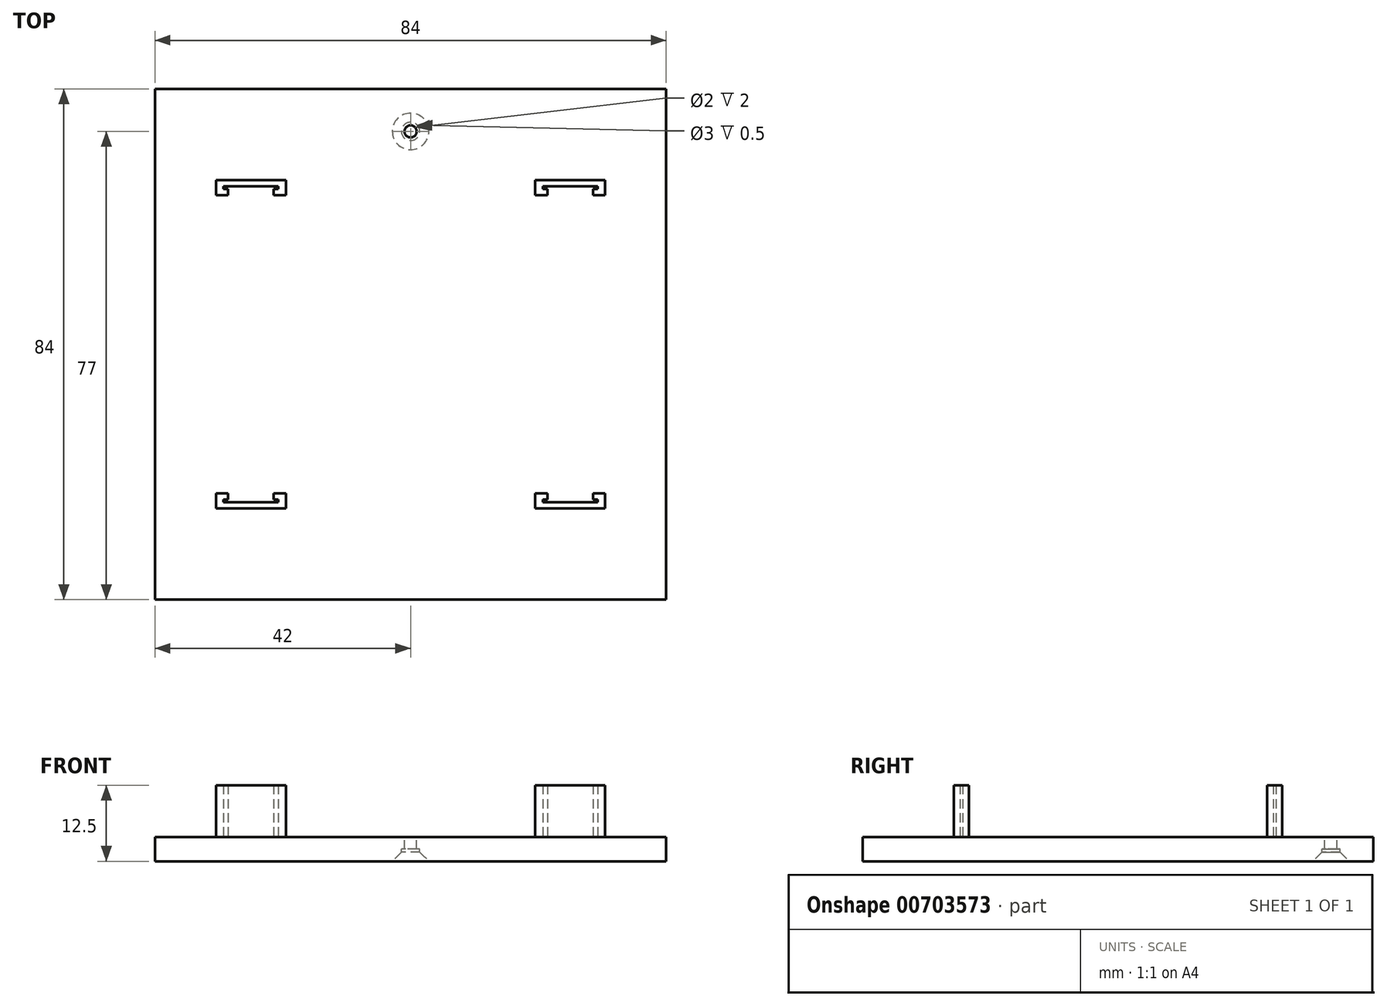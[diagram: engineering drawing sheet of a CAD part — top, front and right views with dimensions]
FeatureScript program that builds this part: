
annotation { "Feature Type Name" : "Feature", "Feature Type Description" : "" }
export const myFeature = defineFeature(function(context is Context, id is Id, definition is map)
    precondition{}
    {
        {
            var Q0;
            Q0=qCreatedBy(makeId("Top.planeOp"),FACE);
            var sketch = newSketch(context, id + "F0", { "sketchPlane" : qUnion([Q0])});
            skLineSegment(sketch, "E0.bottom", {"start": v(-42, 42) * mm, "end": v(42, 42) * mm});
            skLineSegment(sketch, "E0.top", {"start": v(-42, -42) * mm, "end": v(42, -42) * mm});
            skLineSegment(sketch, "E0.left", {"start": v(-42, 42) * mm, "end": v(-42, -42) * mm});
            skLineSegment(sketch, "E0.right", {"start": v(42, 42) * mm, "end": v(42, -42) * mm});
            skSolve(sketch);
        }
        {
            var Q0;
            Q0 = qSketchRegion(id + "F0", true);
            var Q1;
            Q1=makeQuery(id+"F0.imprint","IMPRINT",FACE,{"disambiguationData":[TD([[makeQuery(id+"F0.imprint","IMPRINT",EDGE,{"derivedFrom":sQuery(id+"F0.wireOp",EDGE,"E0.bottom")}),-1.0]])]});
            extrude(context, id + "F1", {"entities" : qUnion([Q0, Q1]), "depth" : 4 * mm, "offsetDistance" : 25 * mm});
        }
        {
            var Q0;
            Q0=makeQuery(id+"F1.opExtrude","CAP_FACE",FACE,{"disambiguationData":[OSD([sQuery(id+"F0.wireOp",EDGE,"E0.bottom"),sQuery(id+"F0.wireOp",EDGE,"E0.top"),sQuery(id+"F0.wireOp",EDGE,"E0.left"),sQuery(id+"F0.wireOp",EDGE,"E0.right")])],"isStart":false});
            var sketch = newSketch(context, id + "F2", { "sketchPlane" : qUnion([Q0])});
            skLineSegment(sketch, "E1.bottom", {"start": v(-32, 27) * mm, "end": v(-30, 27) * mm});
            skLineSegment(sketch, "E1.top", {"start": v(-32, 24.5) * mm, "end": v(-30, 24.5) * mm});
            skLineSegment(sketch, "E1.left", {"start": v(-32, 27) * mm, "end": v(-32, 24.5) * mm});
            skLineSegment(sketch, "E1.right", {"start": v(-30, 27) * mm, "end": v(-30, 24.5) * mm});
            skLineSegment(sketch, "E2.bottom", {"start": v(-22.5, 27) * mm, "end": v(-20.5, 27) * mm});
            skLineSegment(sketch, "E2.top", {"start": v(-22.5, 24.5) * mm, "end": v(-20.5, 24.5) * mm});
            skLineSegment(sketch, "E2.left", {"start": v(-22.5, 27) * mm, "end": v(-22.5, 24.5) * mm});
            skLineSegment(sketch, "E2.right", {"start": v(-20.5, 27) * mm, "end": v(-20.5, 24.5) * mm});
            skLineSegment(sketch, "E3", {"start": v(-30, 27) * mm, "end": v(-22.5, 27) * mm});
            skLineSegment(sketch, "E4", {"start": v(-30, 25.5) * mm, "end": v(-22.5, 25.5) * mm, "construction": true});
            skLineSegment(sketch, "E5", {"start": v(-30, 26) * mm, "end": v(-22.5, 26) * mm});
            skLineSegment(sketch, "E6", {"start": v(-30, 26) * mm, "end": v(-30.75, 26) * mm});
            skLineSegment(sketch, "E7", {"start": v(-30.75, 26) * mm, "end": v(-30.75, 25.5) * mm});
            skLineSegment(sketch, "E8", {"start": v(-30.75, 25.5) * mm, "end": v(-30, 25.5) * mm});
            skLineSegment(sketch, "E9", {"start": v(-22.5, 26) * mm, "end": v(-21.75, 26) * mm});
            skLineSegment(sketch, "E10", {"start": v(-21.75, 26) * mm, "end": v(-21.75, 25.5) * mm});
            skLineSegment(sketch, "E11", {"start": v(-21.75, 25.5) * mm, "end": v(-22.5, 25.5) * mm});
            skLineSegment(sketch, "E12.bottom", {"start": v(-20.5, -27) * mm, "end": v(-22.5, -27) * mm});
            skLineSegment(sketch, "E12.top", {"start": v(-20.5, -24.5) * mm, "end": v(-22.5, -24.5) * mm});
            skLineSegment(sketch, "E12.left", {"start": v(-20.5, -27) * mm, "end": v(-20.5, -24.5) * mm});
            skLineSegment(sketch, "E12.right", {"start": v(-22.5, -27) * mm, "end": v(-22.5, -24.5) * mm});
            skLineSegment(sketch, "E13.bottom", {"start": v(-30, -27) * mm, "end": v(-32, -27) * mm});
            skLineSegment(sketch, "E13.top", {"start": v(-30, -24.5) * mm, "end": v(-32, -24.5) * mm});
            skLineSegment(sketch, "E13.left", {"start": v(-30, -27) * mm, "end": v(-30, -24.5) * mm});
            skLineSegment(sketch, "E13.right", {"start": v(-32, -27) * mm, "end": v(-32, -24.5) * mm});
            skLineSegment(sketch, "E14", {"start": v(-22.5, -27) * mm, "end": v(-30, -27) * mm});
            skLineSegment(sketch, "E15", {"start": v(-22.5, -25.5) * mm, "end": v(-30, -25.5) * mm, "construction": true});
            skLineSegment(sketch, "E16", {"start": v(-22.5, -26) * mm, "end": v(-30, -26) * mm});
            skLineSegment(sketch, "E17", {"start": v(-22.5, -26) * mm, "end": v(-21.75, -26) * mm});
            skLineSegment(sketch, "E18", {"start": v(-21.75, -26) * mm, "end": v(-21.75, -25.5) * mm});
            skLineSegment(sketch, "E19", {"start": v(-21.75, -25.5) * mm, "end": v(-22.5, -25.5) * mm});
            skLineSegment(sketch, "E20", {"start": v(-30, -26) * mm, "end": v(-30.75, -26) * mm});
            skLineSegment(sketch, "E21", {"start": v(-30.75, -26) * mm, "end": v(-30.75, -25.5) * mm});
            skLineSegment(sketch, "E22", {"start": v(-30.75, -25.5) * mm, "end": v(-30, -25.5) * mm});
            skLineSegment(sketch, "E23", {"start": v(-32, 24.5) * mm, "end": v(-32, -24.5) * mm, "construction": true});
            skLineSegment(sketch, "E24.bottom", {"start": v(20.5, 27) * mm, "end": v(22.5, 27) * mm});
            skLineSegment(sketch, "E24.top", {"start": v(20.5, 24.5) * mm, "end": v(22.5, 24.5) * mm});
            skLineSegment(sketch, "E24.left", {"start": v(20.5, 27) * mm, "end": v(20.5, 24.5) * mm});
            skLineSegment(sketch, "E24.right", {"start": v(22.5, 27) * mm, "end": v(22.5, 24.5) * mm});
            skLineSegment(sketch, "E25.bottom", {"start": v(30, 27) * mm, "end": v(32, 27) * mm});
            skLineSegment(sketch, "E25.top", {"start": v(30, 24.5) * mm, "end": v(32, 24.5) * mm});
            skLineSegment(sketch, "E25.left", {"start": v(30, 27) * mm, "end": v(30, 24.5) * mm});
            skLineSegment(sketch, "E25.right", {"start": v(32, 27) * mm, "end": v(32, 24.5) * mm});
            skLineSegment(sketch, "E26", {"start": v(22.5, 27) * mm, "end": v(30, 27) * mm});
            skLineSegment(sketch, "E27", {"start": v(22.5, 25.5) * mm, "end": v(30, 25.5) * mm, "construction": true});
            skLineSegment(sketch, "E28", {"start": v(22.5, 26) * mm, "end": v(30, 26) * mm});
            skLineSegment(sketch, "E29", {"start": v(22.5, 26) * mm, "end": v(21.75, 26) * mm});
            skLineSegment(sketch, "E30", {"start": v(21.75, 26) * mm, "end": v(21.75, 25.5) * mm});
            skLineSegment(sketch, "E31", {"start": v(21.75, 25.5) * mm, "end": v(22.5, 25.5) * mm});
            skLineSegment(sketch, "E32", {"start": v(30, 26) * mm, "end": v(30.75, 26) * mm});
            skLineSegment(sketch, "E33", {"start": v(30.75, 26) * mm, "end": v(30.75, 25.5) * mm});
            skLineSegment(sketch, "E34", {"start": v(30.75, 25.5) * mm, "end": v(30, 25.5) * mm});
            skLineSegment(sketch, "E35.bottom", {"start": v(32, -27) * mm, "end": v(30, -27) * mm});
            skLineSegment(sketch, "E35.top", {"start": v(32, -24.5) * mm, "end": v(30, -24.5) * mm});
            skLineSegment(sketch, "E35.left", {"start": v(32, -27) * mm, "end": v(32, -24.5) * mm});
            skLineSegment(sketch, "E35.right", {"start": v(30, -27) * mm, "end": v(30, -24.5) * mm});
            skLineSegment(sketch, "E36.bottom", {"start": v(22.5, -27) * mm, "end": v(20.5, -27) * mm});
            skLineSegment(sketch, "E36.top", {"start": v(22.5, -24.5) * mm, "end": v(20.5, -24.5) * mm});
            skLineSegment(sketch, "E36.left", {"start": v(22.5, -27) * mm, "end": v(22.5, -24.5) * mm});
            skLineSegment(sketch, "E36.right", {"start": v(20.5, -27) * mm, "end": v(20.5, -24.5) * mm});
            skLineSegment(sketch, "E37", {"start": v(30, -27) * mm, "end": v(22.5, -27) * mm});
            skLineSegment(sketch, "E38", {"start": v(30, -25.5) * mm, "end": v(22.5, -25.5) * mm, "construction": true});
            skLineSegment(sketch, "E39", {"start": v(30, -26) * mm, "end": v(22.5, -26) * mm});
            skLineSegment(sketch, "E40", {"start": v(30, -26) * mm, "end": v(30.75, -26) * mm});
            skLineSegment(sketch, "E41", {"start": v(30.75, -26) * mm, "end": v(30.75, -25.5) * mm});
            skLineSegment(sketch, "E42", {"start": v(30.75, -25.5) * mm, "end": v(30, -25.5) * mm});
            skLineSegment(sketch, "E43", {"start": v(22.5, -26) * mm, "end": v(21.75, -26) * mm});
            skLineSegment(sketch, "E44", {"start": v(21.75, -26) * mm, "end": v(21.75, -25.5) * mm});
            skLineSegment(sketch, "E45", {"start": v(21.75, -25.5) * mm, "end": v(22.5, -25.5) * mm});
            skLineSegment(sketch, "E46", {"start": v(20.5, 24.5) * mm, "end": v(20.5, -24.5) * mm, "construction": true});
            skLineSegment(sketch, "E47", {"start": v(-20.5, 27) * mm, "end": v(20.5, 27) * mm, "construction": true});
            skSolve(sketch);
        }
        {
            var Q0;
            {var subQ1=sQuery(id+"F2.wireOp",EDGE,"E1.bottom");Q0=makeQuery(id+"F2.imprint","IMPRINT",FACE,{"disambiguationData":[TD([[makeQuery(id+"F2.imprint","IMPRINT",EDGE,{"derivedFrom":subQ1}),-1.0]])]});}
            var Q1;
            {var subQ0=sQuery(id+"F2.wireOp",EDGE,"E3");Q1=makeQuery(id+"F2.imprint","IMPRINT",FACE,{"disambiguationData":[TD([[makeQuery(id+"F2.imprint","IMPRINT",EDGE,{"derivedFrom":subQ0}),-1.0]])]});}
            var Q2;
            {var subQ3=sQuery(id+"F2.wireOp",EDGE,"E2.bottom");Q2=makeQuery(id+"F2.imprint","IMPRINT",FACE,{"disambiguationData":[TD([[makeQuery(id+"F2.imprint","IMPRINT",EDGE,{"derivedFrom":subQ3}),-1.0]])]});}
            var Q3;
            {var subQ3=sQuery(id+"F2.wireOp",EDGE,"E13.bottom");Q3=makeQuery(id+"F2.imprint","IMPRINT",FACE,{"disambiguationData":[TD([[makeQuery(id+"F2.imprint","IMPRINT",EDGE,{"derivedFrom":subQ3}),-1.0]])]});}
            var Q4;
            {var subQ0=sQuery(id+"F2.wireOp",EDGE,"E14");Q4=makeQuery(id+"F2.imprint","IMPRINT",FACE,{"disambiguationData":[TD([[makeQuery(id+"F2.imprint","IMPRINT",EDGE,{"derivedFrom":subQ0}),-1.0]])]});}
            var Q5;
            {var subQ1=sQuery(id+"F2.wireOp",EDGE,"E12.bottom");Q5=makeQuery(id+"F2.imprint","IMPRINT",FACE,{"disambiguationData":[TD([[makeQuery(id+"F2.imprint","IMPRINT",EDGE,{"derivedFrom":subQ1}),-1.0]])]});}
            var Q6;
            {var subQ1=sQuery(id+"F2.wireOp",EDGE,"E24.bottom");Q6=makeQuery(id+"F2.imprint","IMPRINT",FACE,{"disambiguationData":[TD([[makeQuery(id+"F2.imprint","IMPRINT",EDGE,{"derivedFrom":subQ1}),-1.0]])]});}
            var Q7;
            {var subQ0=sQuery(id+"F2.wireOp",EDGE,"E26");Q7=makeQuery(id+"F2.imprint","IMPRINT",FACE,{"disambiguationData":[TD([[makeQuery(id+"F2.imprint","IMPRINT",EDGE,{"derivedFrom":subQ0}),-1.0]])]});}
            var Q8;
            {var subQ3=sQuery(id+"F2.wireOp",EDGE,"E25.bottom");Q8=makeQuery(id+"F2.imprint","IMPRINT",FACE,{"disambiguationData":[TD([[makeQuery(id+"F2.imprint","IMPRINT",EDGE,{"derivedFrom":subQ3}),-1.0]])]});}
            var Q9;
            {var subQ3=sQuery(id+"F2.wireOp",EDGE,"E36.bottom");Q9=makeQuery(id+"F2.imprint","IMPRINT",FACE,{"disambiguationData":[TD([[makeQuery(id+"F2.imprint","IMPRINT",EDGE,{"derivedFrom":subQ3}),-1.0]])]});}
            var Q10;
            {var subQ0=sQuery(id+"F2.wireOp",EDGE,"E37");Q10=makeQuery(id+"F2.imprint","IMPRINT",FACE,{"disambiguationData":[TD([[makeQuery(id+"F2.imprint","IMPRINT",EDGE,{"derivedFrom":subQ0}),-1.0]])]});}
            var Q11;
            {var subQ1=sQuery(id+"F2.wireOp",EDGE,"E35.bottom");Q11=makeQuery(id+"F2.imprint","IMPRINT",FACE,{"disambiguationData":[TD([[makeQuery(id+"F2.imprint","IMPRINT",EDGE,{"derivedFrom":subQ1}),-1.0]])]});}
            extrude(context, id + "F3", {"entities" : qUnion([Q0, Q1, Q2, Q3, Q4, Q5, Q6, Q7, Q8, Q9, Q10, Q11]), "operationType" : NewBodyOperationType.ADD, "depth" : 8.5 * mm, "offsetDistance" : 25 * mm});
        }
        {
            var Q0;
            Q0=makeQuery(id+"F1.opExtrude","CAP_FACE",FACE,{"disambiguationData":[OSD([sQuery(id+"F0.wireOp",EDGE,"E0.bottom"),sQuery(id+"F0.wireOp",EDGE,"E0.top"),sQuery(id+"F0.wireOp",EDGE,"E0.left"),sQuery(id+"F0.wireOp",EDGE,"E0.right")])],"isStart":false});
            var sketch = newSketch(context, id + "F4", { "sketchPlane" : qUnion([Q0])});
            skCircle(sketch, "E48", {"center": v(0, 35) * mm, "radius": 1.5 * mm});
            skCircle(sketch, "E49", {"center": v(0, 35) * mm, "radius": 1 * mm});
            skSolve(sketch);
        }
        {
            var Q0;
            Q0=makeQuery(id+"F4.imprint","IMPRINT",FACE,{"disambiguationData":[TD([[makeQuery(id+"F4.imprint","IMPRINT",EDGE,{"derivedFrom":sQuery(id+"F4.wireOp",EDGE,"E49")}),1.0]])]});
            extrude(context, id + "F5", {"entities" : qUnion([Q0]), "operationType" : NewBodyOperationType.REMOVE, "oppositeDirection" : true, "depth" : 25 * mm, "offsetDistance" : 25 * mm});
        }
        {
            var Q0;
            Q0=makeQuery(id+"F4.imprint","IMPRINT",FACE,{"disambiguationData":[TD([[makeQuery(id+"F4.imprint","IMPRINT",EDGE,{"derivedFrom":sQuery(id+"F4.wireOp",EDGE,"E48")}),1.0]])]});
            extrude(context, id + "F6", {"entities" : qUnion([Q0]), "operationType" : NewBodyOperationType.REMOVE, "oppositeDirection" : true, "depth" : 25 * mm, "offsetDistance" : 25 * mm, "hasSecondDirection" : true, "secondDirectionOppositeDirection" : true, "secondDirectionDepth" : 2 * mm});
        }
        {
            var Q0;
            Q0=makeQuery(id+"F6.boolean.opBoolean","INTERSECT",EDGE,{"derivedFrom":[makeQuery(id+"F1.opExtrude","CAP_FACE",FACE,{"disambiguationData":[OSD([sQuery(id+"F0.wireOp",EDGE,"E0.bottom"),sQuery(id+"F0.wireOp",EDGE,"E0.top"),sQuery(id+"F0.wireOp",EDGE,"E0.left"),sQuery(id+"F0.wireOp",EDGE,"E0.right")])],"isStart":true}),makeQuery(id+"F6.opExtrude","SWEPT_FACE",FACE,{"disambiguationData":[OSD([sQuery(id+"F4.wireOp",EDGE,"E48")])]})]});
            chamfer(context, id + "F7", {"entities" : qUnion([Q0]), "width" : 1.5 * mm, "tangentPropagation" : true});
        }
    });
